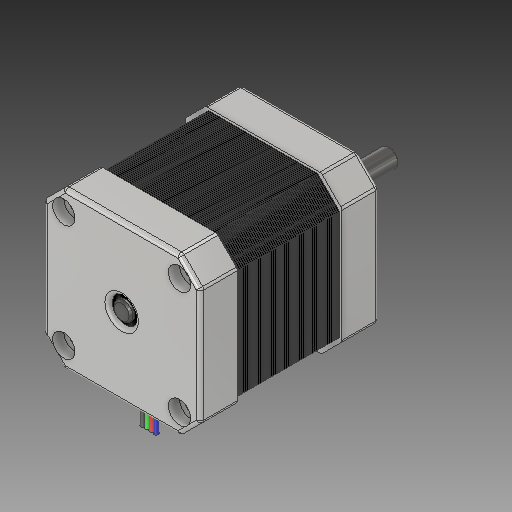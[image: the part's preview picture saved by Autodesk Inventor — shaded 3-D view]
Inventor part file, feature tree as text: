
AUTODESK INVENTOR PART (.ipt)
format: ipt  version: 2017 (Build 210142000, 142)  size: 1,355,264 bytes
history: native  units: mm
features: sketch x5, other x3
ambient origin geometry x8: Origin, YZ Plane, XZ Plane, XY Plane, X Axis, Y Axis, Z Axis, Center Point
bodies: Solid1 (feature_tree)
feature tree (8):
  other  "Nema17.ipt"
  other  "Solid1::Nema17.ipt"
  other  "TaggingFeature1"
  sketch  "Sketch1"  dims[d0=10.0mm]
  sketch  "Sketch4"
  sketch  "Sketch5"
  sketch  "Sketch6"
  sketch  "Sketch11"
